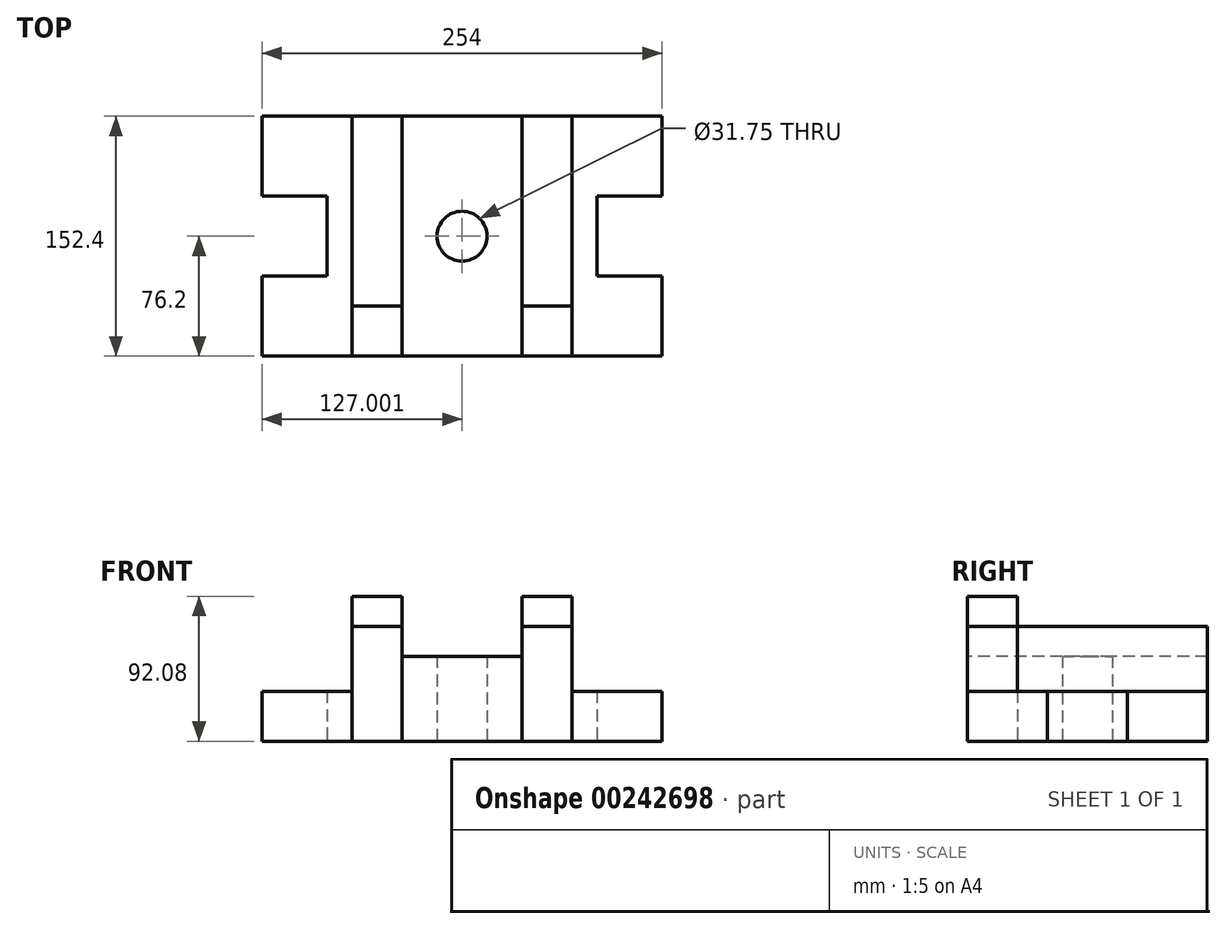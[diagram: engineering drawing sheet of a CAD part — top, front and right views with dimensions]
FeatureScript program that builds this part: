
annotation { "Feature Type Name" : "Feature", "Feature Type Description" : "" }
export const myFeature = defineFeature(function(context is Context, id is Id, definition is map)
    precondition{}
    {
        {
            var Q0;
            Q0=qCreatedBy(makeId("Top.planeOp"),FACE);
            var sketch = newSketch(context, id + "F0", { "sketchPlane" : qUnion([Q0])});
            skLineSegment(sketch, "E0.bottom", {"start": v(-109.07, 76.2) * mm, "end": v(144.93, 76.2) * mm});
            skLineSegment(sketch, "E0.top", {"start": v(-109.07, -76.2) * mm, "end": v(144.93, -76.2) * mm});
            skLineSegment(sketch, "E0.left", {"start": v(-109.07, 76.2) * mm, "end": v(-109.07, -76.2) * mm});
            skLineSegment(sketch, "E0.right", {"start": v(144.93, 76.2) * mm, "end": v(144.93, -76.2) * mm});
            skLineSegment(sketch, "E1.bottom", {"start": v(103.66, 25.4) * mm, "end": v(144.93, 25.4) * mm});
            skLineSegment(sketch, "E1.top", {"start": v(103.66, -25.4) * mm, "end": v(144.93, -25.4) * mm});
            skLineSegment(sketch, "E1.left", {"start": v(103.66, 25.4) * mm, "end": v(103.66, -25.4) * mm});
            skLineSegment(sketch, "E1.right", {"start": v(144.93, 25.4) * mm, "end": v(144.93, -25.4) * mm});
            skLineSegment(sketch, "E2.bottom", {"start": v(-109.07, 25.4) * mm, "end": v(-67.8, 25.4) * mm});
            skLineSegment(sketch, "E2.top", {"start": v(-109.07, -25.4) * mm, "end": v(-67.8, -25.4) * mm});
            skLineSegment(sketch, "E2.left", {"start": v(-109.07, 25.4) * mm, "end": v(-109.07, -25.4) * mm});
            skLineSegment(sketch, "E2.right", {"start": v(-67.8, 25.4) * mm, "end": v(-67.8, -25.4) * mm});
            skLineSegment(sketch, "E3.bottom", {"start": v(-51.92, 76.2) * mm, "end": v(-20.17, 76.2) * mm});
            skLineSegment(sketch, "E3.top", {"start": v(-51.92, -76.2) * mm, "end": v(-20.17, -76.2) * mm});
            skLineSegment(sketch, "E3.left", {"start": v(-51.92, 76.2) * mm, "end": v(-51.92, -76.2) * mm});
            skLineSegment(sketch, "E3.right", {"start": v(-20.17, 76.2) * mm, "end": v(-20.17, -76.2) * mm});
            skLineSegment(sketch, "E4.bottom", {"start": v(56.03, 76.2) * mm, "end": v(87.78, 76.2) * mm});
            skLineSegment(sketch, "E4.top", {"start": v(56.03, -76.2) * mm, "end": v(87.78, -76.2) * mm});
            skLineSegment(sketch, "E4.left", {"start": v(56.03, 76.2) * mm, "end": v(56.03, -76.2) * mm});
            skLineSegment(sketch, "E4.right", {"start": v(87.78, 76.2) * mm, "end": v(87.78, -76.2) * mm});
            skLineSegment(sketch, "E5.top", {"start": v(-51.92, 44.45) * mm, "end": v(-20.17, 44.45) * mm});
            skLineSegment(sketch, "E5.left", {"start": v(-51.92, 76.2) * mm, "end": v(-51.92, 44.45) * mm});
            skLineSegment(sketch, "E5.right", {"start": v(-20.17, 76.2) * mm, "end": v(-20.17, 44.45) * mm});
            skLineSegment(sketch, "E6.bottom", {"start": v(-51.92, -44.45) * mm, "end": v(-20.17, -44.45) * mm});
            skLineSegment(sketch, "E6.left", {"start": v(-51.92, -44.45) * mm, "end": v(-51.92, -76.2) * mm});
            skLineSegment(sketch, "E6.right", {"start": v(-20.17, -44.45) * mm, "end": v(-20.17, -76.2) * mm});
            skLineSegment(sketch, "E7.top", {"start": v(56.03, 44.45) * mm, "end": v(87.78, 44.45) * mm});
            skLineSegment(sketch, "E7.left", {"start": v(56.03, 76.2) * mm, "end": v(56.03, 44.45) * mm});
            skLineSegment(sketch, "E7.right", {"start": v(87.78, 76.2) * mm, "end": v(87.78, 44.45) * mm});
            skLineSegment(sketch, "E8.bottom", {"start": v(56.03, -44.45) * mm, "end": v(87.78, -44.45) * mm});
            skLineSegment(sketch, "E8.left", {"start": v(56.03, -44.45) * mm, "end": v(56.03, -76.2) * mm});
            skLineSegment(sketch, "E8.right", {"start": v(87.78, -44.45) * mm, "end": v(87.78, -76.2) * mm});
            skCircle(sketch, "E9", {"center": v(17.93, 0) * mm, "radius": 15.88 * mm});
            skSolve(sketch);
        }
        {
            var Q0;
            {var subQ5=sQuery(id+"F0.wireOp",EDGE,"E2.bottom");Q0=makeQuery(id+"F0.imprint","IMPRINT",FACE,{"disambiguationData":[TD([[makeQuery(id+"F0.imprint","IMPRINT",EDGE,{"derivedFrom":subQ5}),1.0]])]});}
            extrude(context, id + "F1", {"entities" : qUnion([Q0]), "depth" : 31.75 * mm});
        }
        {
            var Q0;
            {var subQ8=sQuery(id+"F0.wireOp",EDGE,"E1.bottom");Q0=makeQuery(id+"F0.imprint","IMPRINT",FACE,{"disambiguationData":[TD([[makeQuery(id+"F0.imprint","IMPRINT",EDGE,{"derivedFrom":subQ8}),1.0]])]});}
            extrude(context, id + "F2", {"entities" : qUnion([Q0]), "depth" : 31.75 * mm});
        }
        {
            var Q0;
            Q0=makeQuery(id+"F0.imprint","IMPRINT",FACE,{"disambiguationData":[TD([[makeQuery(id+"F0.imprint","IMPRINT",EDGE,{"derivedFrom":sQuery(id+"F0.wireOp",EDGE,"E6.bottom")}),-1.0]])]});
            var Q1;
            Q1=makeQuery(id+"F0.imprint","IMPRINT",FACE,{"disambiguationData":[TD([[makeQuery(id+"F0.imprint","IMPRINT",EDGE,{"derivedFrom":sQuery(id+"F0.wireOp",EDGE,"E3.bottom")}),-1.0]])]});
            var Q2;
            Q2=makeQuery(id+"F0.imprint","IMPRINT",FACE,{"disambiguationData":[TD([[makeQuery(id+"F0.imprint","IMPRINT",EDGE,{"derivedFrom":sQuery(id+"F0.wireOp",EDGE,"E4.bottom")}),-1.0]])]});
            var Q3;
            Q3=makeQuery(id+"F0.imprint","IMPRINT",FACE,{"disambiguationData":[TD([[makeQuery(id+"F0.imprint","IMPRINT",EDGE,{"derivedFrom":sQuery(id+"F0.wireOp",EDGE,"E8.bottom")}),-1.0]])]});
            extrude(context, id + "F3", {"entities" : qUnion([Q0, Q1, Q2, Q3]), "depth" : 92.07 * mm});
        }
        {
            var Q0;
            Q0=makeQuery(id+"F0.imprint","IMPRINT",FACE,{"disambiguationData":[TD([[makeQuery(id+"F0.imprint","IMPRINT",EDGE,{"derivedFrom":sQuery(id+"F0.wireOp",EDGE,"E3.left")}),1.0]])]});
            var Q1;
            Q1=makeQuery(id+"F0.imprint","IMPRINT",FACE,{"disambiguationData":[TD([[makeQuery(id+"F0.imprint","IMPRINT",EDGE,{"derivedFrom":sQuery(id+"F0.wireOp",EDGE,"E4.left")}),1.0]])]});
            extrude(context, id + "F4", {"entities" : qUnion([Q0, Q1]), "depth" : 73.02 * mm});
        }
        {
            var Q0;
            Q0=makeQuery(id+"F0.imprint","IMPRINT",FACE,{"disambiguationData":[TD([[makeQuery(id+"F0.imprint","IMPRINT",EDGE,{"derivedFrom":sQuery(id+"F0.wireOp",EDGE,"E3.right")}),1.0]])]});
            extrude(context, id + "F5", {"entities" : qUnion([Q0]), "depth" : 53.97 * mm});
        }
    });
